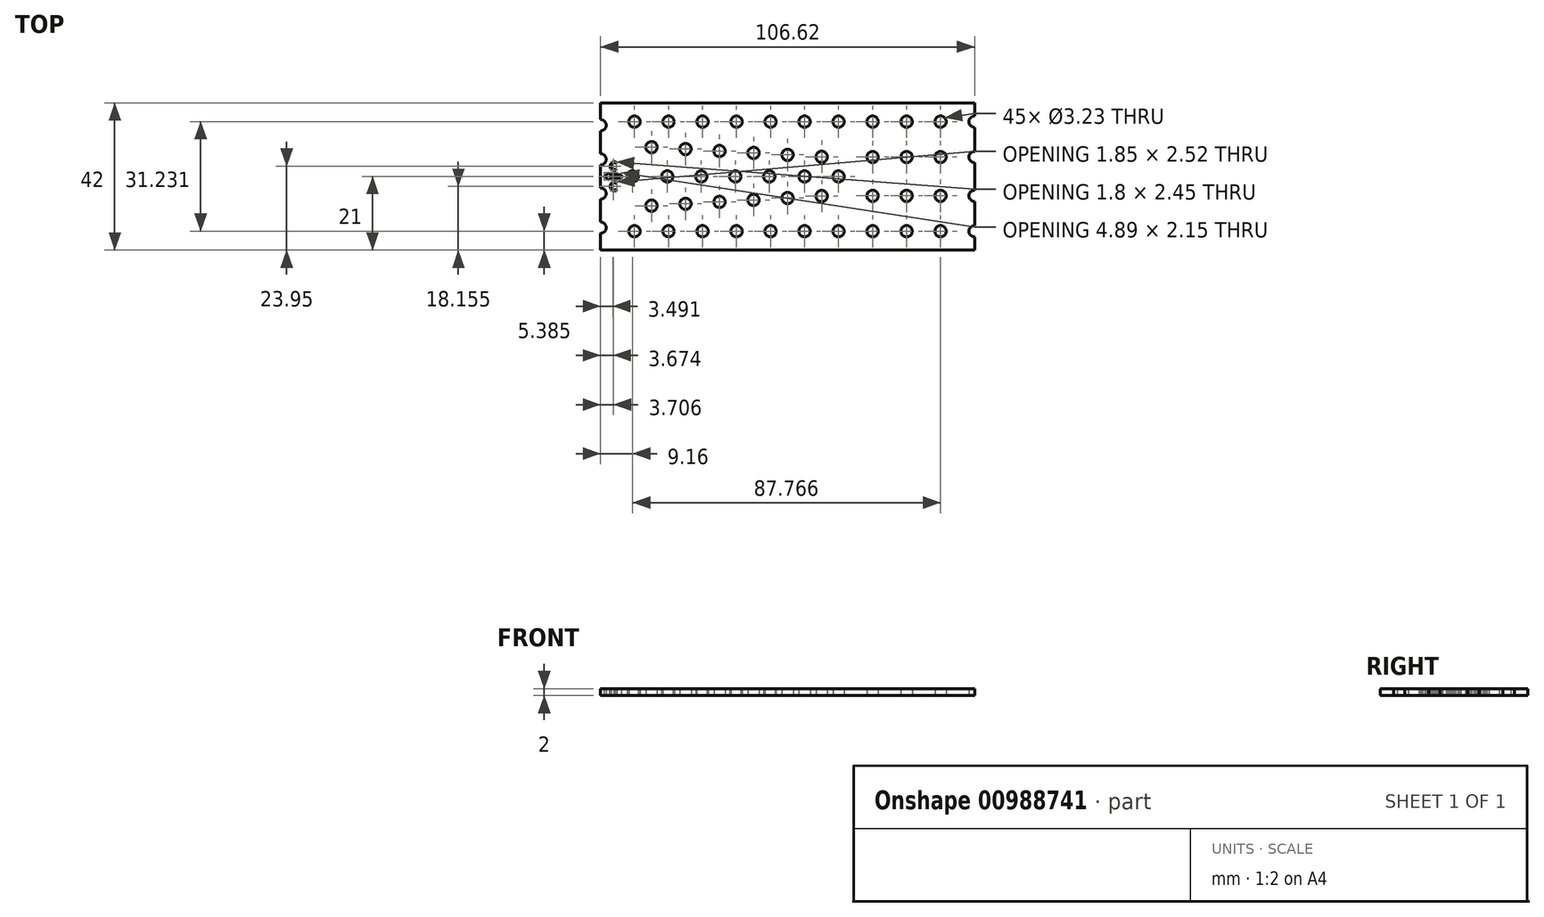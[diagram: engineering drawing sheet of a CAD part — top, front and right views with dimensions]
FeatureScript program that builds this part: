
annotation { "Feature Type Name" : "Feature", "Feature Type Description" : "" }
export const myFeature = defineFeature(function(context is Context, id is Id, definition is map)
    precondition{}
    {
        {
            var Q0;
            Q0=qCreatedBy(makeId("Top.planeOp"),FACE);
            var sketch = newSketch(context, id + "F0", { "sketchPlane" : qUnion([Q0])});
            skLineSegment(sketch, "E0", {"start": v(-53.3, 21) * mm, "end": v(53.3, 21) * mm});
            skLineSegment(sketch, "E1", {"start": v(53.3, 21) * mm, "end": v(53.3, 17.23) * mm});
            skLineSegment(sketch, "E2", {"start": v(-53.3, -21) * mm, "end": v(53.3, -21) * mm});
            skLineSegment(sketch, "E3", {"start": v(-53.3, 21) * mm, "end": v(-53.3, 16.22) * mm});
            skLineSegment(sketch, "E4", {"start": v(53.3, 14) * mm, "end": v(53.3, 7.14) * mm});
            skArc(sketch, "E5", {"start": v(-53.3, 12.98) * mm, "mid": v(-51.7, 14.6) * mm, "end": v(-53.3, 16.22) * mm});
            skArc(sketch, "E6", {"start": v(-53.3, 3.27) * mm, "mid": v(-51.7, 4.88) * mm, "end": v(-53.3, 6.5) * mm});
            skCircle(sketch, "E7", {"center": v(-43.62, 15.62) * mm, "radius": 1.62 * mm});
            skCircle(sketch, "E8", {"center": v(-38.77, 8.34) * mm, "radius": 1.62 * mm});
            skCircle(sketch, "E9", {"center": v(-29.08, 7.8) * mm, "radius": 1.62 * mm});
            skCircle(sketch, "E10", {"center": v(-19.38, 7.26) * mm, "radius": 1.62 * mm});
            skCircle(sketch, "E11", {"center": v(-9.7, 6.7) * mm, "radius": 1.62 * mm});
            skCircle(sketch, "E12", {"center": v(0, 6.15) * mm, "radius": 1.62 * mm});
            skCircle(sketch, "E13", {"center": v(9.73, 5.6) * mm, "radius": 1.62 * mm});
            skCircle(sketch, "E14", {"center": v(24.23, 5.53) * mm, "radius": 1.62 * mm});
            skCircle(sketch, "E15", {"center": v(-33.92, 15.62) * mm, "radius": 1.62 * mm});
            skCircle(sketch, "E16", {"center": v(-24.23, 15.62) * mm, "radius": 1.62 * mm});
            skCircle(sketch, "E17", {"center": v(-14.54, 15.62) * mm, "radius": 1.62 * mm});
            skCircle(sketch, "E18", {"center": v(-4.85, 15.62) * mm, "radius": 1.62 * mm});
            skCircle(sketch, "E19", {"center": v(4.85, 15.62) * mm, "radius": 1.62 * mm});
            skCircle(sketch, "E20", {"center": v(14.54, 15.62) * mm, "radius": 1.62 * mm});
            skCircle(sketch, "E21", {"center": v(24.23, 15.62) * mm, "radius": 1.62 * mm});
            skCircle(sketch, "E22", {"center": v(33.92, 15.62) * mm, "radius": 1.62 * mm});
            skCircle(sketch, "E23", {"center": v(43.62, 15.62) * mm, "radius": 1.62 * mm});
            skArc(sketch, "E24", {"start": v(53.3, 17.23) * mm, "mid": v(51.7, 15.62) * mm, "end": v(53.3, 14) * mm});
            skCircle(sketch, "E25", {"center": v(33.92, 5.53) * mm, "radius": 1.62 * mm});
            skCircle(sketch, "E26", {"center": v(43.62, 5.53) * mm, "radius": 1.62 * mm});
            skArc(sketch, "E27", {"start": v(53.3, 7.14) * mm, "mid": v(51.7, 5.53) * mm, "end": v(53.3, 3.91) * mm});
            skCircle(sketch, "E28", {"center": v(-44.15, 0) * mm, "radius": 1.62 * mm});
            skCircle(sketch, "E29", {"center": v(-34.28, 0) * mm, "radius": 1.62 * mm});
            skCircle(sketch, "E30", {"center": v(-24.58, 0) * mm, "radius": 1.62 * mm});
            skCircle(sketch, "E31", {"center": v(-14.9, 0) * mm, "radius": 1.62 * mm});
            skCircle(sketch, "E32", {"center": v(-5.2, 0) * mm, "radius": 1.62 * mm});
            skCircle(sketch, "E33", {"center": v(4.85, 0) * mm, "radius": 1.62 * mm});
            skCircle(sketch, "E34", {"center": v(14.54, 0) * mm, "radius": 1.62 * mm});
            skLineSegment(sketch, "E35", {"start": v(-53.3, 12.98) * mm, "end": v(-53.3, 6.5) * mm});
            skLineSegment(sketch, "E36", {"start": v(53.3, -21) * mm, "end": v(53.3, -17.23) * mm});
            skLineSegment(sketch, "E37", {"start": v(53.3, -14) * mm, "end": v(53.3, -7.14) * mm});
            skLineSegment(sketch, "E38", {"start": v(-53.3, -21) * mm, "end": v(-53.3, -16.22) * mm});
            skLineSegment(sketch, "E39", {"start": v(-53.3, -12.98) * mm, "end": v(-53.3, -6.5) * mm});
            skArc(sketch, "E40", {"start": v(-53.3, -16.22) * mm, "mid": v(-51.7, -14.6) * mm, "end": v(-53.3, -12.98) * mm});
            skArc(sketch, "E41", {"start": v(-53.3, -6.5) * mm, "mid": v(-51.7, -4.88) * mm, "end": v(-53.3, -3.27) * mm});
            skCircle(sketch, "E42", {"center": v(-43.62, -15.62) * mm, "radius": 1.62 * mm});
            skCircle(sketch, "E43", {"center": v(-38.77, -8.34) * mm, "radius": 1.62 * mm});
            skCircle(sketch, "E44", {"center": v(-29.08, -7.8) * mm, "radius": 1.62 * mm});
            skCircle(sketch, "E45", {"center": v(-19.38, -7.26) * mm, "radius": 1.62 * mm});
            skCircle(sketch, "E46", {"center": v(-9.7, -6.7) * mm, "radius": 1.62 * mm});
            skCircle(sketch, "E47", {"center": v(0, -6.15) * mm, "radius": 1.62 * mm});
            skCircle(sketch, "E48", {"center": v(9.73, -5.6) * mm, "radius": 1.62 * mm});
            skCircle(sketch, "E49", {"center": v(24.23, -5.53) * mm, "radius": 1.62 * mm});
            skCircle(sketch, "E50", {"center": v(-33.92, -15.62) * mm, "radius": 1.62 * mm});
            skCircle(sketch, "E51", {"center": v(-24.23, -15.62) * mm, "radius": 1.62 * mm});
            skCircle(sketch, "E52", {"center": v(-14.54, -15.62) * mm, "radius": 1.62 * mm});
            skCircle(sketch, "E53", {"center": v(-4.85, -15.62) * mm, "radius": 1.62 * mm});
            skCircle(sketch, "E54", {"center": v(4.85, -15.62) * mm, "radius": 1.62 * mm});
            skCircle(sketch, "E55", {"center": v(14.54, -15.62) * mm, "radius": 1.62 * mm});
            skCircle(sketch, "E56", {"center": v(24.23, -15.62) * mm, "radius": 1.62 * mm});
            skCircle(sketch, "E57", {"center": v(33.92, -15.62) * mm, "radius": 1.62 * mm});
            skCircle(sketch, "E58", {"center": v(43.62, -15.62) * mm, "radius": 1.62 * mm});
            skArc(sketch, "E59", {"start": v(53.3, -14) * mm, "mid": v(51.7, -15.62) * mm, "end": v(53.3, -17.23) * mm});
            skCircle(sketch, "E60", {"center": v(33.92, -5.53) * mm, "radius": 1.62 * mm});
            skCircle(sketch, "E61", {"center": v(43.62, -5.53) * mm, "radius": 1.62 * mm});
            skArc(sketch, "E62", {"start": v(53.3, -3.91) * mm, "mid": v(51.7, -5.53) * mm, "end": v(53.3, -7.14) * mm});
            skLineSegment(sketch, "E63", {"start": v(-53.3, -3.27) * mm, "end": v(-53.3, 3.27) * mm});
            skLineSegment(sketch, "E64", {"start": v(53.3, -3.91) * mm, "end": v(53.3, 3.91) * mm});
            skLineSegment(sketch, "E65", {"start": v(-52.27, 0) * mm, "end": v(-50.77, 1.08) * mm});
            skLineSegment(sketch, "E66", {"start": v(-50.77, 1.08) * mm, "end": v(-50.77, 0.54) * mm});
            skLineSegment(sketch, "E67", {"start": v(-47.37, 0.54) * mm, "end": v(-47.37, -0.54) * mm});
            skLineSegment(sketch, "E68", {"start": v(-50.77, 0.54) * mm, "end": v(-47.37, 0.54) * mm});
            skLineSegment(sketch, "E69", {"start": v(-50.77, -0.54) * mm, "end": v(-47.37, -0.54) * mm});
            skLineSegment(sketch, "E70", {"start": v(-52.27, 0) * mm, "end": v(-50.77, -1.08) * mm});
            skLineSegment(sketch, "E71", {"start": v(-50.77, -1.08) * mm, "end": v(-50.77, -0.54) * mm});
            skText(sketch, "E72", { "text": "C", "fontName": "OpenSans-Regular.ttf"});
            skText(sketch, "E73", { "text": "C", "fontName": "OpenSans-Regular.ttf"});
            const initialGuessF0  = {"E72": [-0.05074, 0.00176, 1, 0, 0.0024], "E73": [-0.05074, -0.00407, 1, 0, 0.00247]};
            skSetInitialGuess(sketch, initialGuessF0);
            skSolve(sketch);
        }
        {
            var Q0;
            Q0=makeQuery(id+"F0.imprint","IMPRINT",FACE,{"disambiguationData":[TD([[makeQuery(id+"F0.imprint","IMPRINT",EDGE,{"derivedFrom":sQuery(id+"F0.wireOp",EDGE,"E0")}),-1.0]])]});
            extrude(context, id + "F1", {"entities" : qUnion([Q0]), "depth" : 2 * mm, "offsetDistance" : 25 * mm});
        }
    });
